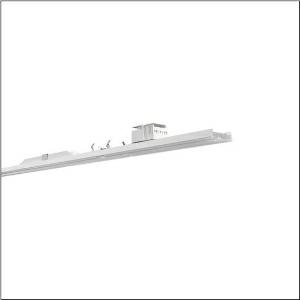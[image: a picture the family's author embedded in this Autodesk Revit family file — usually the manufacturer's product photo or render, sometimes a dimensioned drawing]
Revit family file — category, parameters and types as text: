
# Revit family: licross_r__11_recessed_extreme_ho_51tl12dn4dxle_e724
name_source: partatom
category: Lighting Fixtures
units: mm (PartAtom-declared; Revit-internal decimal feet)

## family parameters
Cut with Voids When Loaded = No
Host = Face
Light Source = No
Part Type = Normal
Room Calculation Point = No
Round Connector Dimension = Use Diameter
Shared = No

## types (1)
- --- (1 x LED, 13000 lm, 75.1 W, 4000K)
    Apparent Load = 75 VA
    CIE Flux Codes = 66 91 98 100 100
    Color Rendering = 80
    Color Temperature = 4000K
    Default Elevation = 1800 mm
    Description = Licross® 11 Recessed extreme HOluminaire insert, length: 1.500mm, width: 66mm, height: 67mm, LED rated luminous flux: 13.000lm, light colour: 840, control gear: DALI 2, control gear: ECG DALI, with plug, 5-pole, with phase selection, mains connection: 220..240V, AC, 50/60Hz, halogen-free wiring, primary optical cover: cover, of PMMA, light emission: direct distribution, protection rating (complete): IP40, insulation class (complete): insulation class I (protective earthing), certification: CE, ENEC, VDE, protection symbol: D if used in an environment without relevant dust loads with corresponding accessories, permissible ambient temperature for indoor applications: -25..+45°C, reducing of maximum allowable ambient temperature of 5°C with ceiling mounting, corresponds to IFS (International Featured Standards) requirements for safety and quality in the food industry, packaging unit: 1 piece
    Height = 58 mm
    Lamp = 1 x LED
    Lamp Light Flux = 13000 lm
    Lamp Power = 75.1 W
    Lamp count = 1
    Length = 1500 mm
    Luminous efficacy = 173 lm/W
    Manufacturer = Siteco
    ModVariant = No
    Model = 51TL12DN4DXLE
    Mounting Place = Ceiling
    Mounting Type = Pendant
    Number of Poles = 1
    OnlyDefault = Yes
    Power Factor = 1
    Product Name = Licross® 11 Recessed extreme HO
    Product group = luminaire insert
    ProductGroupID = 902
    Protection Class = Protection class I
    Protection Degree = IP 40
    RLX_Detail_Level = 1
    RlxData = <blob elided: 22213 chars, md5=ad9e920b>
    Socket = socket
    Standby Power = 0 W
    System Light Flux = 13000 lm
    System Power = 75 W
    Type Comments = factory setting: luminous flux: 100 % | dim-lin: 254 | 425 mA
    Type Image = l_1266722.jpg
    URL = http://relux.com
    VarID = @adj_132594
    Voltage = 0 V
    Weight = 0.00 kg
    Width = 66 mm

## geometry (parser evidence)
native form markers: Blend x4, Sweep x12
no freeform markers — native parametric forms only
